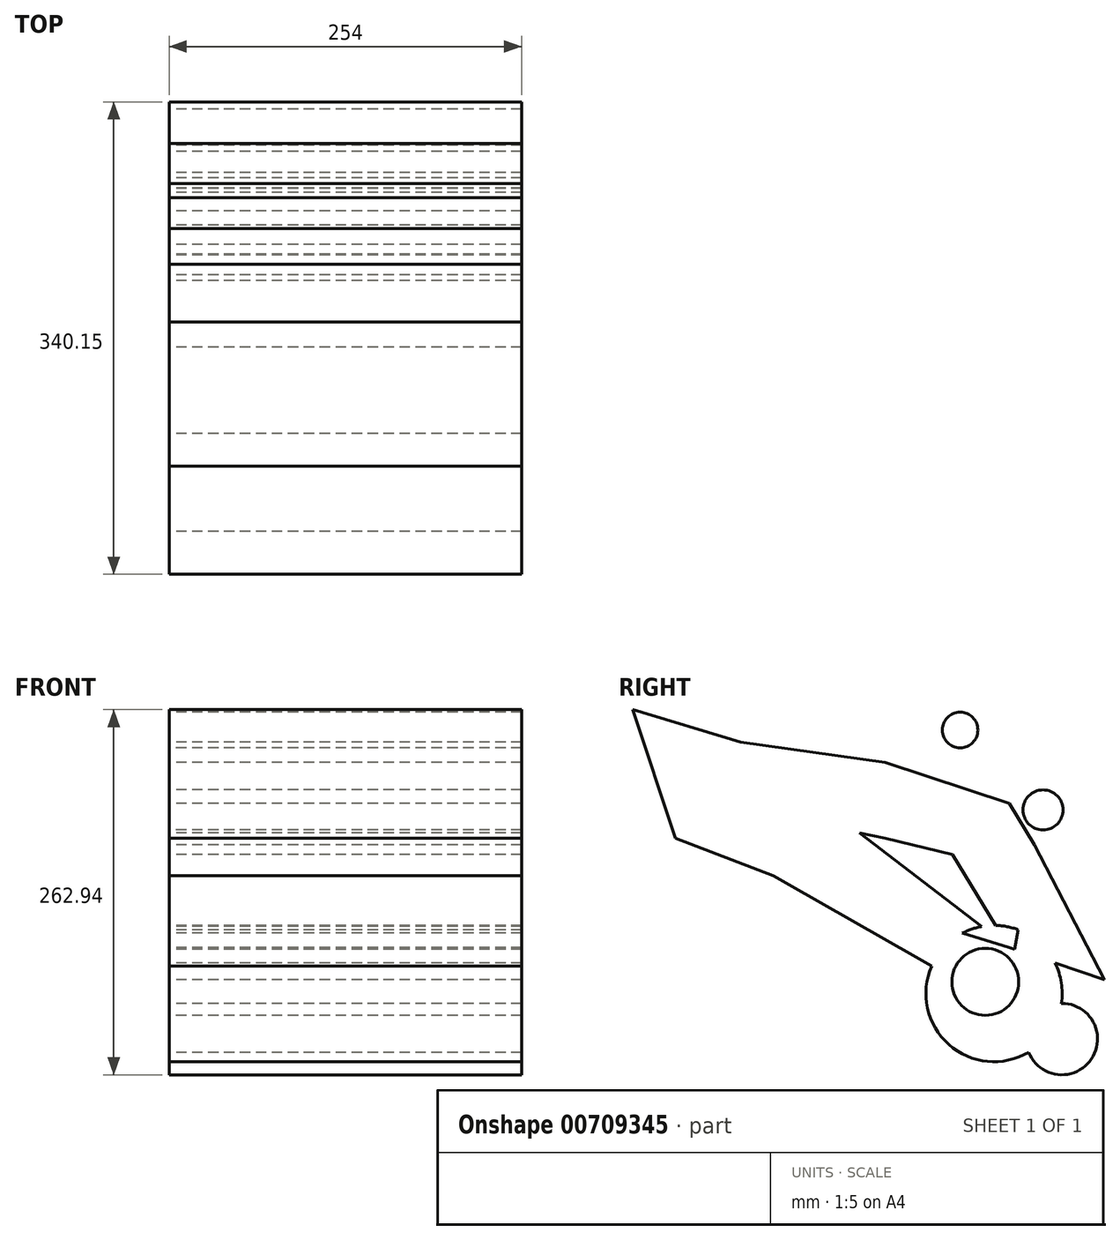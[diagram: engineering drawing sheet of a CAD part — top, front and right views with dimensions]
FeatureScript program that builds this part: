
annotation { "Feature Type Name" : "Feature", "Feature Type Description" : "" }
export const myFeature = defineFeature(function(context is Context, id is Id, definition is map)
    precondition{}
    {
        {
            var Q0;
            Q0=qCreatedBy(makeId("Right.planeOp"),FACE);
            var sketch = newSketch(context, id + "F0", { "sketchPlane" : qUnion([Q0])});
            skLineSegment(sketch, "E0", {"start": v(-490.78, 252.96) * mm, "end": v(-396.7, 178.24) * mm});
            skLineSegment(sketch, "E1", {"start": v(-396.7, 178.24) * mm, "end": v(-308.94, 160.48) * mm});
            skLineSegment(sketch, "E2", {"start": v(-308.94, 160.48) * mm, "end": v(-308.94, 214.9) * mm});
            skLineSegment(sketch, "E3", {"start": v(-308.94, 214.9) * mm, "end": v(-260.09, 148.59) * mm});
            skLineSegment(sketch, "E4", {"start": v(-260.09, 148.59) * mm, "end": v(-308.94, 160.48) * mm});
            skLineSegment(sketch, "E5", {"start": v(-490.78, 252.96) * mm, "end": v(-412.98, 229.73) * mm});
            skLineSegment(sketch, "E6", {"start": v(-412.98, 229.73) * mm, "end": v(-389.46, 133.36) * mm});
            skLineSegment(sketch, "E7", {"start": v(-389.46, 133.36) * mm, "end": v(-219.38, 81.75) * mm});
            skLineSegment(sketch, "E8", {"start": v(-219.38, 81.75) * mm, "end": v(-412.98, 229.73) * mm});
            skLineSegment(sketch, "E9", {"start": v(-412.98, 229.73) * mm, "end": v(-308.94, 214.9) * mm});
            skLineSegment(sketch, "E10", {"start": v(-260.09, 148.59) * mm, "end": v(-219.38, 81.75) * mm});
            skLineSegment(sketch, "E11", {"start": v(-490.78, 252.96) * mm, "end": v(-460.02, 160.48) * mm});
            skLineSegment(sketch, "E12", {"start": v(-460.02, 160.48) * mm, "end": v(-389.46, 133.36) * mm});
            skLineSegment(sketch, "E13", {"start": v(-260.09, 148.59) * mm, "end": v(-254.04, 191.03) * mm});
            skLineSegment(sketch, "E14", {"start": v(-255.57, 191.24) * mm, "end": v(-201.29, 155.75) * mm});
            skLineSegment(sketch, "E15", {"start": v(-201.29, 155.75) * mm, "end": v(-219.38, 185.45) * mm});
            skLineSegment(sketch, "E16", {"start": v(-308.94, 214.9) * mm, "end": v(-219.38, 185.45) * mm});
            skLineSegment(sketch, "E17", {"start": v(-201.29, 155.75) * mm, "end": v(-260.09, 148.59) * mm});
            skLineSegment(sketch, "E18", {"start": v(-201.29, 155.75) * mm, "end": v(-150.63, 58.34) * mm});
            skLineSegment(sketch, "E19", {"start": v(-150.63, 58.34) * mm, "end": v(-219.38, 81.75) * mm});
            skLineSegment(sketch, "E20", {"start": v(-215.76, 79.42) * mm, "end": v(-201.29, 155.75) * mm});
            skLineSegment(sketch, "E21", {"start": v(-389.46, 133.36) * mm, "end": v(-268.23, 64.39) * mm});
            skCircle(sketch, "E22", {"center": v(-254.66, 238.32) * mm, "radius": 12.78 * mm});
            skCircle(sketch, "E23", {"center": v(-194.95, 180.79) * mm, "radius": 14.44 * mm});
            skCircle(sketch, "E24", {"center": v(-236.57, 56.91) * mm, "radius": 24.1 * mm});
            skCircle(sketch, "E25", {"center": v(-181.38, 15.74) * mm, "radius": 25.72 * mm});
            skCircle(sketch, "E26", {"center": v(-230.24, 48.52) * mm, "radius": 49.1 * mm});
            skPoint(sketch, "E27", {"position": v(-357.8, 48.58) * mm});
            skPoint(sketch, "E28", {"position": v(0, -93.08) * mm});
            skPoint(sketch, "E29", {"position": v(-383.12, 72.21) * mm});
            skSolve(sketch);
        }
        {
            var Q0;
            Q0 = qSketchRegion(id + "F0", true);
            extrude(context, id + "F1", {"entities" : qUnion([Q0]), "depth" : 254 * mm, "offsetDistance" : 25.4 * mm});
        }
    });
